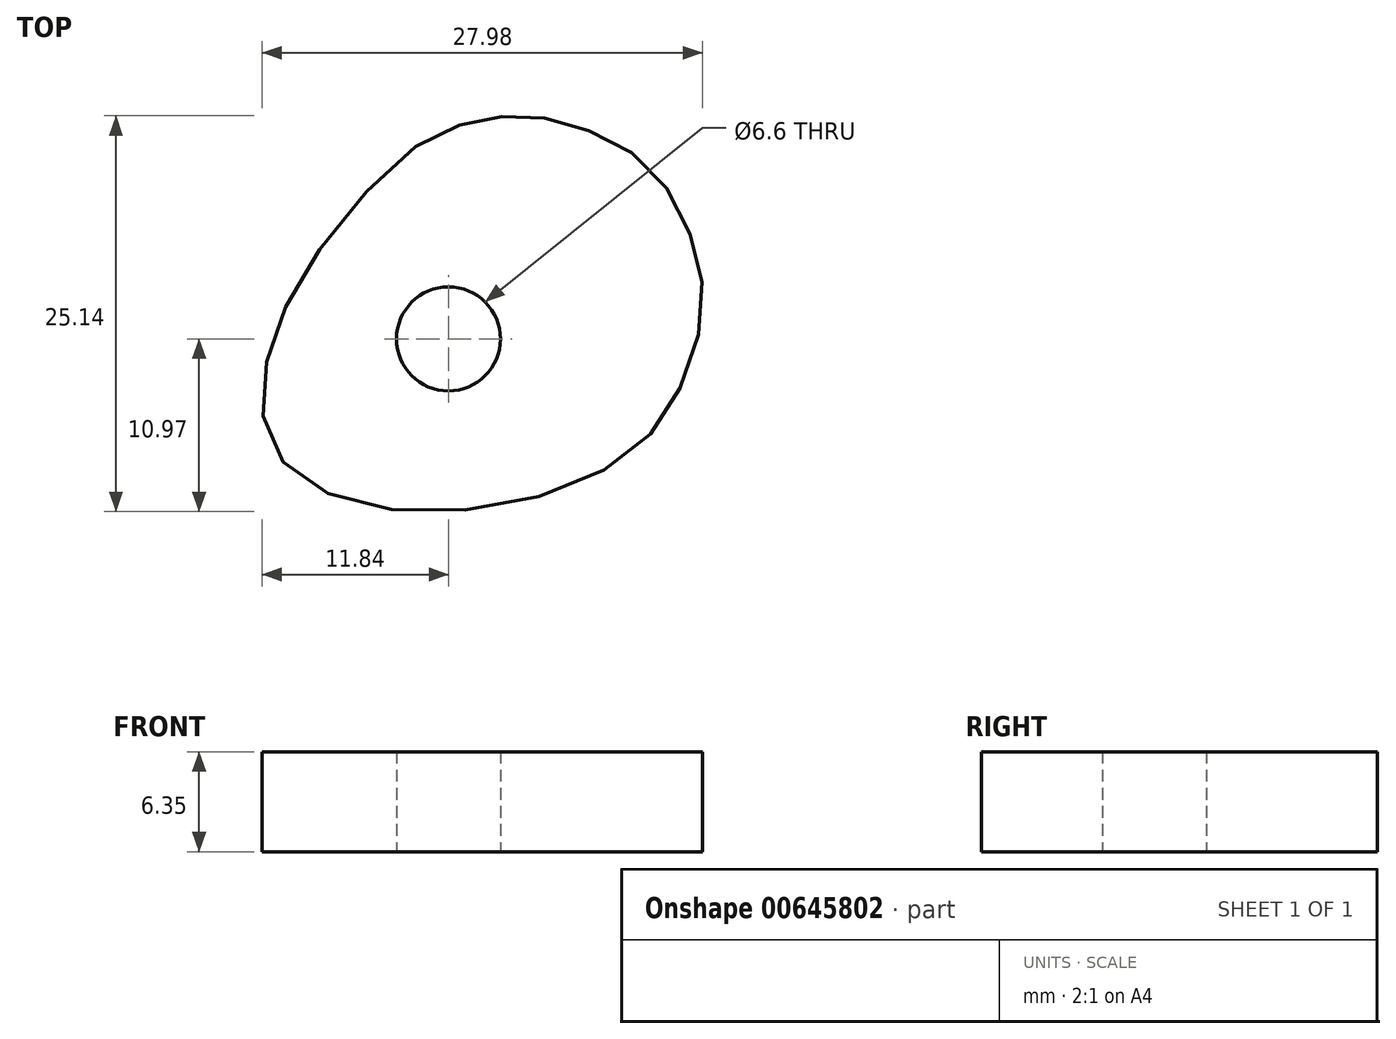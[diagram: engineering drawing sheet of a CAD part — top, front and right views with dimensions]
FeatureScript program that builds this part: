
annotation { "Feature Type Name" : "Feature", "Feature Type Description" : "" }
export const myFeature = defineFeature(function(context is Context, id is Id, definition is map)
    precondition{}
    {
        {
            var Q0;
            Q0=qCreatedBy(makeId("Top.planeOp"),FACE);
            var sketch = newSketch(context, id + "F0", { "sketchPlane" : qUnion([Q0])});
            skFitSpline(sketch, "E0", {"points": [v(-11.57, -1.47) * mm, v(-8.62, 5) * mm, v(-2.28, 12.08) * mm, v(1.7, 13.85) * mm, v(5.08, 14.14) * mm, v(8.77, 13.26) * mm, v(12.6, 11.05) * mm, v(15.25, 6.92) * mm, v(16.13, 2.36) * mm, v(14.66, -3.24) * mm, v(10.98, -7.66) * mm, v(2.14, -10.76) * mm, v(-7.15, -10.02) * mm, v(-11.27, -6.63) * mm, v(-11.57, -1.47) * mm]});
            skCircle(sketch, "E1", {"center": v(0, 0) * mm, "radius": 3.3 * mm});
            skSolve(sketch);
        }
        {
            var Q0;
            Q0=makeQuery(id+"F0.imprint","IMPRINT",FACE,{"disambiguationData":[TD([[makeQuery(id+"F0.imprint","IMPRINT",EDGE,{"derivedFrom":sQuery(id+"F0.wireOp",EDGE,"E0")}),-1.0]])]});
            extrude(context, id + "F1", {"entities" : qUnion([Q0]), "depth" : 6.35 * mm, "offsetDistance" : 25.4 * mm});
        }
    });
